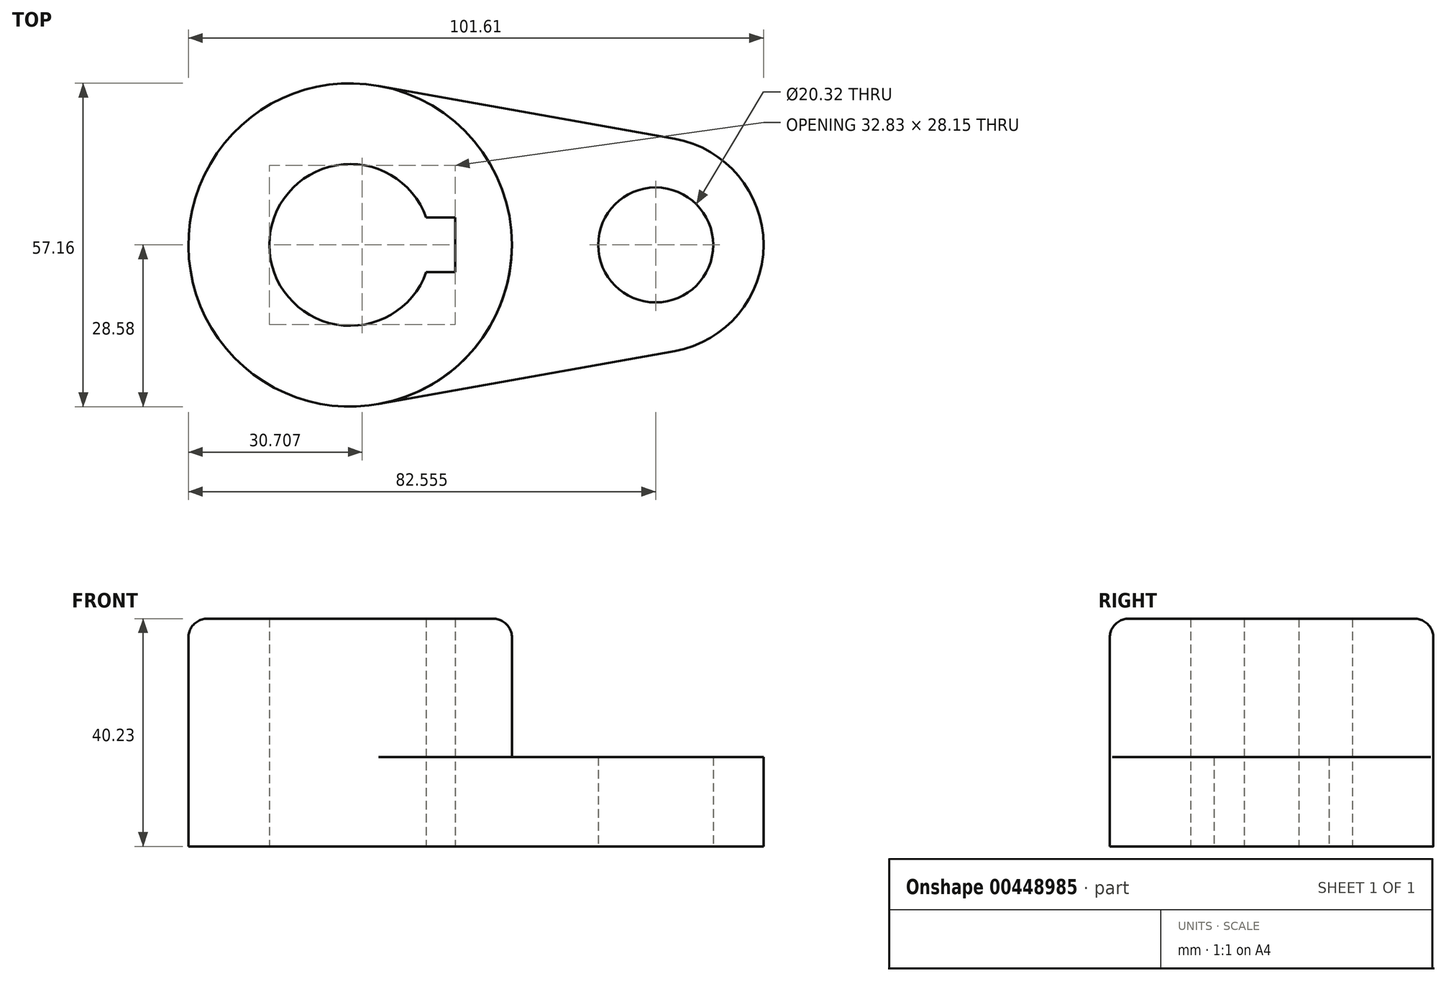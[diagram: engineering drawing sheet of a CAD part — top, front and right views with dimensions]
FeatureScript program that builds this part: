
annotation { "Feature Type Name" : "Feature", "Feature Type Description" : "" }
export const myFeature = defineFeature(function(context is Context, id is Id, definition is map)
    precondition{}
    {
        {
            var Q0;
            Q0=qCreatedBy(makeId("Top.planeOp"),FACE);
            var sketch = newSketch(context, id + "F0", { "sketchPlane" : qUnion([Q0])});
            skArc(sketch, "E0", {"start": v(57.34, -18.75) * mm, "mid": v(73.03, 0) * mm, "end": v(57.34, 18.75) * mm});
            skLineSegment(sketch, "E1", {"start": v(5.04, 28.13) * mm, "end": v(57.34, 18.75) * mm});
            skLineSegment(sketch, "E2", {"start": v(5.04, -28.13) * mm, "end": v(57.34, -18.75) * mm});
            skArc(sketch, "E3", {"start": v(13.45, 4.83) * mm, "mid": v(-14.29, 0) * mm, "end": v(13.45, -4.83) * mm});
            skLineSegment(sketch, "E4", {"start": v(13.45, 4.83) * mm, "end": v(18.54, 4.83) * mm});
            skLineSegment(sketch, "E5", {"start": v(18.54, 4.83) * mm, "end": v(18.54, -4.83) * mm});
            skLineSegment(sketch, "E6", {"start": v(18.54, -4.83) * mm, "end": v(13.45, -4.83) * mm});
            skCircle(sketch, "E7", {"center": v(53.98, 0) * mm, "radius": 10.16 * mm});
            skCircle(sketch, "E8.converted", {"center": v(0, 0) * mm, "radius": 28.58 * mm});
            skSolve(sketch);
        }
        {
            var Q0;
            Q0=makeQuery(id+"F0.imprint","IMPRINT",FACE,{"disambiguationData":[TD([[makeQuery(id+"F0.imprint","IMPRINT",EDGE,{"derivedFrom":sQuery(id+"F0.wireOp",EDGE,"E3")}),-1.0]])]});
            extrude(context, id + "F1", {"entities" : qUnion([Q0]), "depth" : 40.23 * mm});
        }
        {
            var Q0;
            Q0=makeQuery(id+"F0.imprint","IMPRINT",FACE,{"disambiguationData":[TD([[makeQuery(id+"F0.imprint","IMPRINT",EDGE,{"derivedFrom":sQuery(id+"F0.wireOp",EDGE,"E0")}),1.0]])]});
            extrude(context, id + "F2", {"entities" : qUnion([Q0]), "operationType" : NewBodyOperationType.ADD, "depth" : 15.77 * mm});
        }
        {
            var Q0;
            Q0=makeQuery(id+"F1.opExtrude","CAP_EDGE",EDGE,{"disambiguationData":[OSD([sQuery(id+"F0.wireOp",EDGE,"E8.converted")])],"isStart":false});
            fillet(context, id + "F3", {"entities" : qUnion([Q0]), "radius" : 3.3 * mm, "tangentPropagation" : true, "allowEdgeOverflow" : false});
        }
    });
